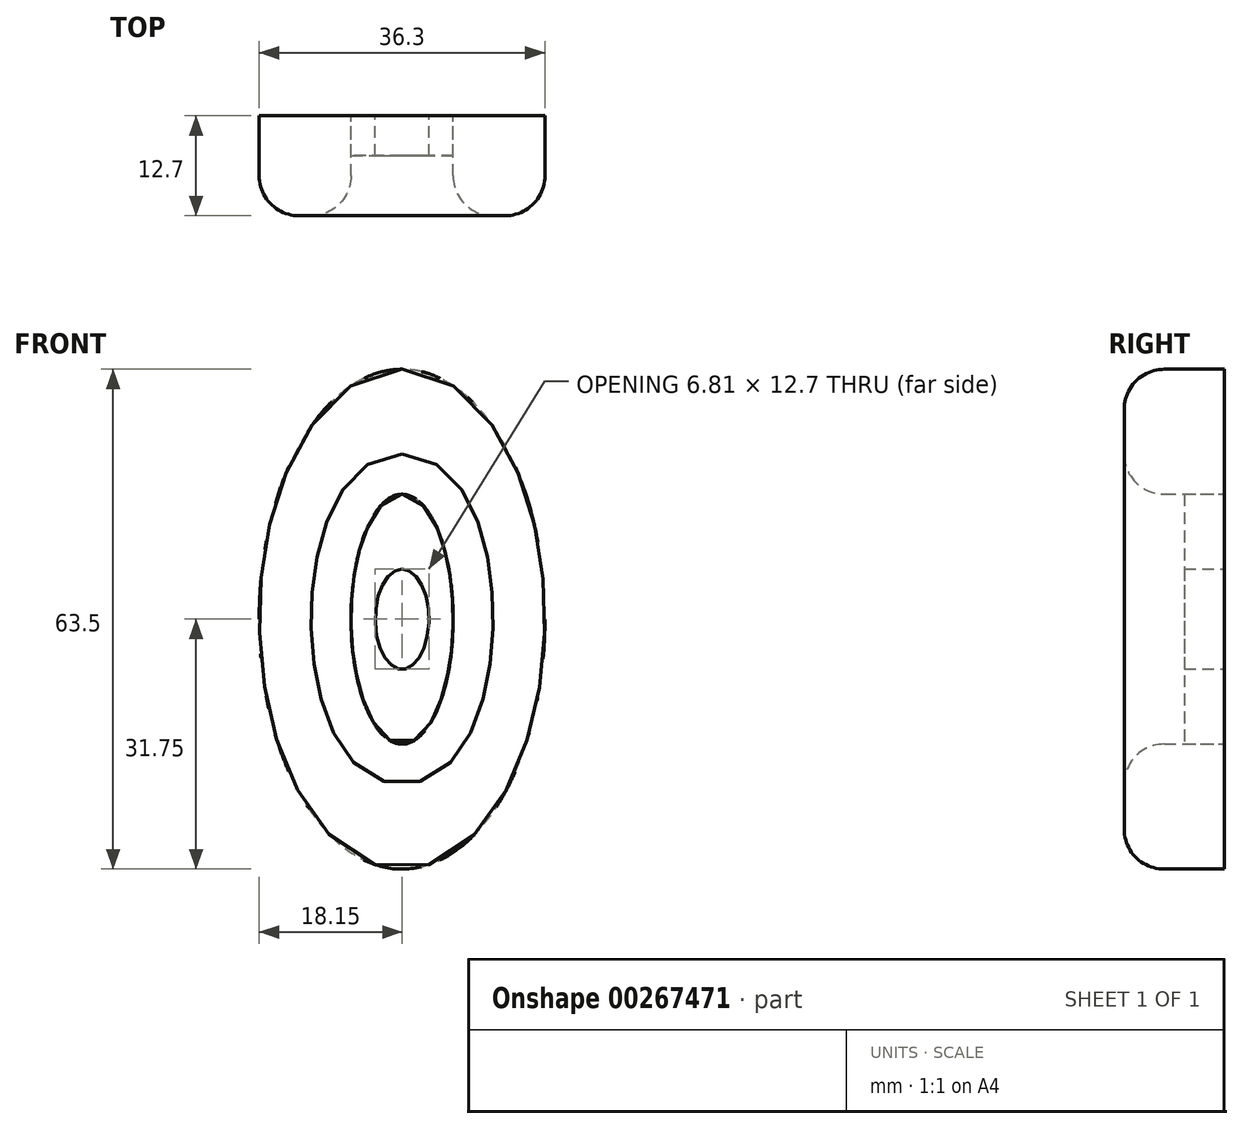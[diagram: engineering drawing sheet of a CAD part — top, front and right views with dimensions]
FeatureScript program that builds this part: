
annotation { "Feature Type Name" : "Feature", "Feature Type Description" : "" }
export const myFeature = defineFeature(function(context is Context, id is Id, definition is map)
    precondition{}
    {
        {
            var Q0;
            Q0=qCreatedBy(makeId("Front.planeOp"),FACE);
            var sketch = newSketch(context, id + "F0", { "sketchPlane" : qUnion([Q0])});
            skEllipse(sketch, "E0", {"center": v(0, 0) * mm, "majorRadius": 31.75 * mm, "minorRadius": 18.15 * mm, "majorAxis": v(0, 1)});
            skEllipse(sketch, "E1", {"center": v(0, 0) * mm, "majorRadius": 15.88 * mm, "minorRadius": 6.49 * mm, "majorAxis": v(0, 1)});
            skEllipse(sketch, "E2", {"center": v(0, 0) * mm, "majorRadius": 6.35 * mm, "minorRadius": 3.4 * mm, "majorAxis": v(0, 1)});
            skSolve(sketch);
        }
        {
            var Q0;
            Q0 = qSketchRegion(id + "F0", true);
            extrude(context, id + "F1", {"entities" : qUnion([Q0]), "depth" : 12.7 * mm});
        }
        {
            var Q0;
            Q0=makeQuery(id+"F0.imprint","IMPRINT",FACE,{"disambiguationData":[TD([[makeQuery(id+"F0.imprint","IMPRINT",EDGE,{"derivedFrom":sQuery(id+"F0.wireOp",EDGE,"E1")}),1.0]])]});
            extrude(context, id + "F2", {"entities" : qUnion([Q0]), "depth" : 5.08 * mm});
        }
        {
            var Q0;
            Q0=makeQuery(id+"F1.opExtrude","CAP_EDGE",EDGE,{"disambiguationData":[OSD([sQuery(id+"F0.wireOp",EDGE,"E0")])],"isStart":false});
            var Q1;
            Q1=makeQuery(id+"F1.opExtrude","CAP_EDGE",EDGE,{"disambiguationData":[OSD([sQuery(id+"F0.wireOp",EDGE,"E1")])],"isStart":false});
            fillet(context, id + "F3", {"entities" : qUnion([Q0, Q1]), "radius" : 5.08 * mm, "tangentPropagation" : true, "allowEdgeOverflow" : false});
        }
    });
